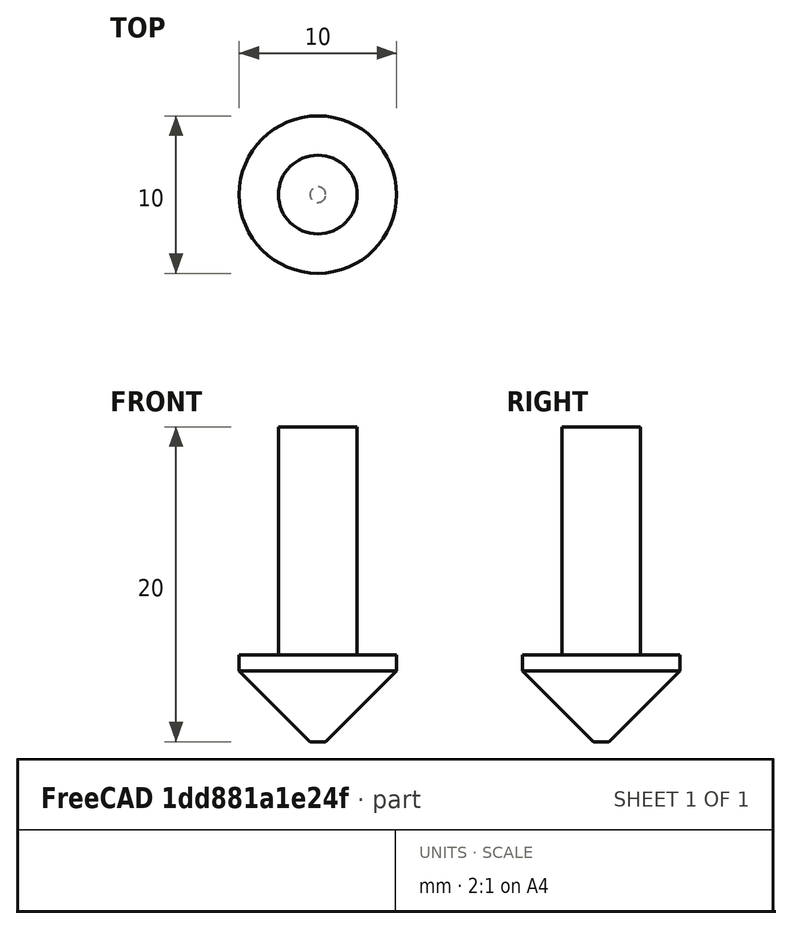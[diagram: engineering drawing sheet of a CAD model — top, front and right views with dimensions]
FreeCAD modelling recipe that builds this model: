
FCSTD DOCUMENT  (FreeCAD 1.0R39109 (Git))
Label: v-bit
License: Creative Commons Attribution 4.0
LicenseURL: https://creativecommons.org/licenses/by/4.0/
objects: Sketcher::SketchObject×1, PartDesign::Revolution×1, App::FeaturePython×1, PartDesign::Body×1
note: 6 computed .brp shape members not serialized (recipe doc carries the construction recipe); baked Part::Feature solids carry a one-line shape summary decoded from their .brp

FEATURE [Sketcher::SketchObject] Sketch
  ArcFitTolerance = 0
  AttachmentSupport = -> [XZ_Plane]
  FullyConstrained = true
  MakeInternals = false
  MapMode = 5
  Placement = pos=(0,0,0) rot=(1,0,0;1.5708rad)
  expr: Constraints[17] = <<Attributes>>.Diameter
  expr: Constraints[18] = <<Attributes>>.CuttingEdgeAngle
  expr: Constraints[19] = <<Attributes>>.Length
  expr: Constraints[22] = <<Attributes>>.ShankDiameter
  expr: Constraints[26] = <<Attributes>>.CuttingEdgeHeight
  expr: Constraints[28] = <<Attributes>>.TipDiameter
  sketch-geometry (12):
    g0: LineSegment StartX=0 StartY=20 StartZ=0 EndX=0 EndY=0 EndZ=0
    g1: LineSegment StartX=0 StartY=0 StartZ=0 EndX=0.5 EndY=0 EndZ=0
    g2: LineSegment StartX=0.5 StartY=0 StartZ=0 EndX=5 EndY=4.5 EndZ=0
    g3: LineSegment StartX=5 StartY=5.5 StartZ=0 EndX=2.5 EndY=5.49 EndZ=0
    g4: LineSegment StartX=2.5 StartY=5.49 StartZ=0 EndX=2.5 EndY=20 EndZ=0
    g5: LineSegment StartX=2.5 StartY=20 StartZ=0 EndX=0 EndY=20 EndZ=0
    g6: LineSegment [constr] StartX=-5 StartY=4.5 StartZ=0 EndX=5 EndY=4.5 EndZ=0
    g7: LineSegment [constr] StartX=5 StartY=4.5 StartZ=0 EndX=0.5 EndY=0 EndZ=0
    g8: LineSegment [constr] StartX=0.5 StartY=0 StartZ=0 EndX=-0.5 EndY=0 EndZ=0
    g9: LineSegment [constr] StartX=-0.5 StartY=0 StartZ=0 EndX=-5 EndY=4.5 EndZ=0
    g10: LineSegment [constr] StartX=2.5 StartY=20 StartZ=0 EndX=-2.5 EndY=20 EndZ=0
    g11: LineSegment StartX=5 StartY=4.5 StartZ=0 EndX=5 EndY=5.5 EndZ=0
  constraints (30):
    c: Vertical(g0)
    c: Coincident(g0,g1)
    c: Horizontal(g1)
    c: Coincident(g1,g2)
    c: Coincident(g3,g4)
    c: Vertical(g4)
    c: Coincident(g4,g5)
    c: Horizontal(g5)
    c: Coincident(g5,g0)
    c: Coincident(g6,g7)
    c: Coincident(g7,g8)
    c: Coincident(g8,g9)
    c: Coincident(g9,g6)
    c: Symmetric(g8,g7,g0)
    c: Coincident(g1,g7)
    c: Coincident(g2,g6)
    c: Symmetric(g2,g6,g0)
    c: DistanceX(g6,g6) = 10
    c: Angle(g2,g9) = 1.5708
    c: DistanceY(g0,g0) = 20
    c: Coincident(g10,g4)
    c: Symmetric(g10,g4,g-2)
    c: DistanceX(g10,g10) = 5
    c: Vertical(g11)
    c: Coincident(g3,g11)
    c: Coincident(g11,g2)
    c: DistanceY(g11,g11) = 1
    c: Coincident(g-1,g0)
    c: DistanceX(g8,g8) = 1
    c: DistanceY(g3,g3) = 0.01
FEATURE [PartDesign::Revolution] Revolution
  AllowMultiFace = false
  Angle = 360
  Angle2 = 60
  Axis = (0,2e-16,1)
  Base = (0,0,0)
  Placement = pos=(0,0,0) rot=(1,0,0;1.5708rad)
  Profile = -> Sketch
  ReferenceAxis = -> Sketch [V_Axis]
  Reversed = true
  Suppressed = false
  Type = 0
FEATURE [App::FeaturePython] PropertyBag  label="Attributes"  # WARN: FeaturePython — macro-defined, semantics opaque (R4)
  CustomPropertyGroups = 0
  CuttingEdgeAngle = 90
  CuttingEdgeHeight = 1
  Diameter = 10
  Flutes = 2
  Length = 20
  ShankDiameter = 5
  TipDiameter = 1
FEATURE [PartDesign::Body] Body  label="VBit"
  AllowCompound = false
  Group = -> [Sketch,Revolution,PropertyBag]
  Origin = -> Origin
  Tip = -> Revolution
